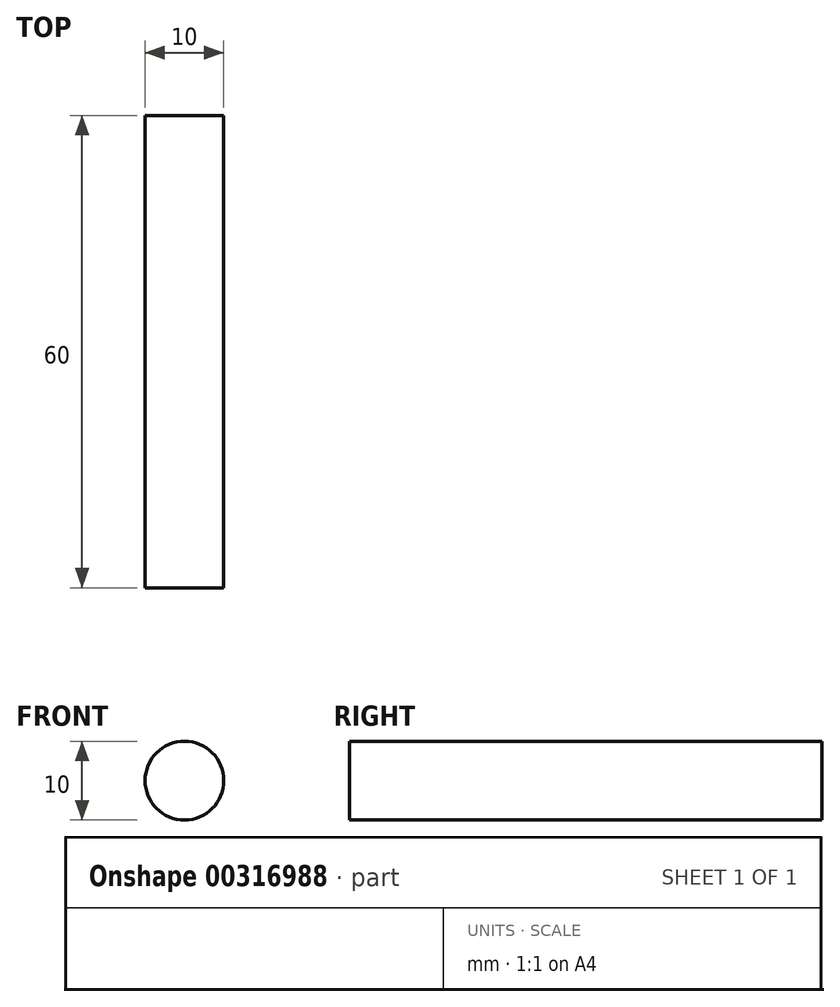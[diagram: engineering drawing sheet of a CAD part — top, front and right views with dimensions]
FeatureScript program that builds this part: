
annotation { "Feature Type Name" : "Feature", "Feature Type Description" : "" }
export const myFeature = defineFeature(function(context is Context, id is Id, definition is map)
    precondition{}
    {
        {
            var Q0;
            Q0=qCreatedBy(makeId("Front.planeOp"),FACE);
            var sketch = newSketch(context, id + "F0", { "sketchPlane" : qUnion([Q0])});
            skCircle(sketch, "E0", {"center": v(-34.02, 27.07) * mm, "radius": 5 * mm});
            skSolve(sketch);
        }
        {
            var Q0;
            Q0=makeQuery(id+"F0.imprint","IMPRINT",FACE,{"disambiguationData":[TD([[makeQuery(id+"F0.imprint","IMPRINT",EDGE,{"derivedFrom":sQuery(id+"F0.wireOp",EDGE,"E0")}),1.0]])]});
            extrude(context, id + "F1", {"entities" : qUnion([Q0]), "depth" : 60 * mm});
        }
    });
